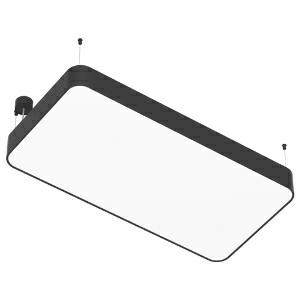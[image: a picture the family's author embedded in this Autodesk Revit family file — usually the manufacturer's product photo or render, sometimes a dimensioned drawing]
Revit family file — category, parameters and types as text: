
# Revit family: smoothy_41180
name_source: partatom
category: Leuchten
revit_build: Autodesk Revit 2016 (Build: 20190508_0715(x64)
units: mm (PartAtom-declared; Revit-internal decimal feet)

## family parameters
Basisbauteil = Fläche
Beim Laden mit Abzugskörper schneiden = Nein
Bemaßung runder Anschluss = Durchmesser verwenden
Gemeinsam genutzt = Nein
Lichtquelle = Nein
Raumberechnungspunkt = Nein
Teiletyp = Normal

## types (1)
- 41180-D01 (8 x LED, 1880 lm, 11.2 W, 3000K)
    Approval mark = CE
    Beschreibung = SMOOTHY
    CIE Flux Codes = 47 78 95 100 74
    Color Rendering = 1B/80…89
    Color Temperature = 3000K
    Height = 120 mm
    Hersteller = Prolicht
    Lamp Light Flux = 1880 lm
    Lamp Power = 11.2 W
    Lamp count = 8
    Lampe = 8 x LED
    Length = 1200 mm
    Luminous efficacy = 124 lm/W
    ModVariant = Nein
    Modell = 41180
    Mounting Place = Ceiling
    Mounting Type = Pendant
    Number of Poles = 1
    OnlyDefault = Ja
    Power Factor = 1
    Product Name = SMOOTHY
    Product group = Suspended lights
    ProductGroupID = 941
    Protection Class = Protection class I
    Protection Degree = IP 20
    RLX_Detail_Level = 1
    RlxData = <blob elided: 31701 chars, md5=499b2d92>
    Scheinlast = 90 VA
    Socket = socket
    Standby Power = 0 W
    System Light Flux = 11145 lm
    System Power = 90 W
    Typenbild = 41180.jpg
    Typenkommentare = DIFFUSER Opal (01)
    URL = http://relux.com
    VarID = 41180-d01
    Voltage = 0 V
    Vorgabe-Ansicht = 1800 mm
    Weight = 0.00 kg
    Width = 600 mm

## geometry (parser evidence)
native form markers: Blend x4, Sweep x13
no freeform markers — native parametric forms only
